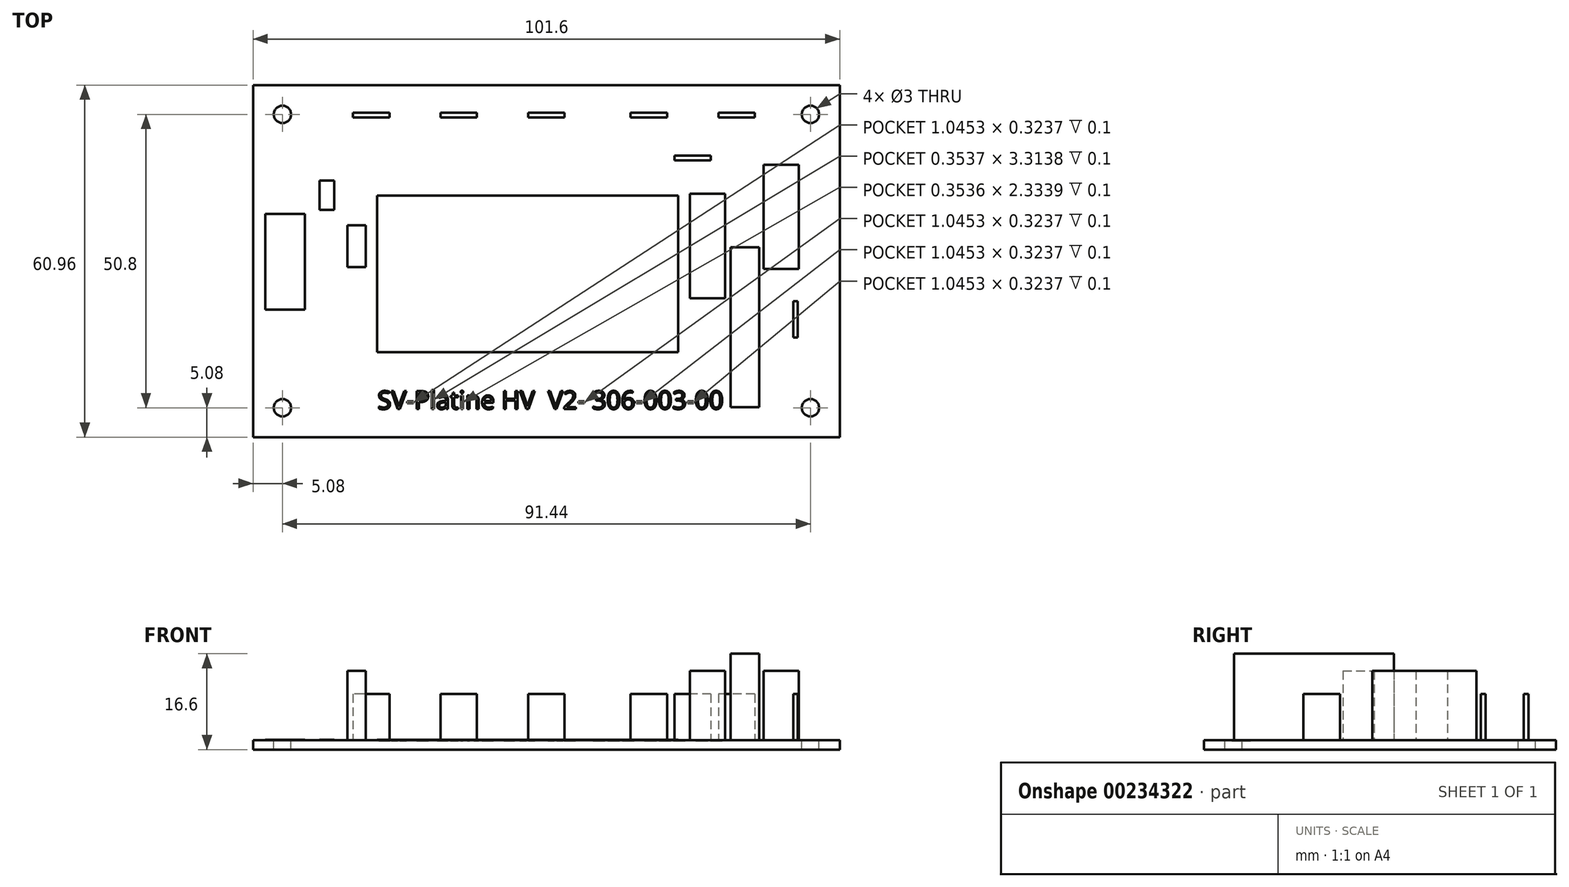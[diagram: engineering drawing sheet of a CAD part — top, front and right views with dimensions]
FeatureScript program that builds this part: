
annotation { "Feature Type Name" : "Feature", "Feature Type Description" : "" }
export const myFeature = defineFeature(function(context is Context, id is Id, definition is map)
    precondition{}
    {
        {
            var Q0;
            Q0=qCreatedBy(makeId("Top.planeOp"),FACE);
            var sketch = newSketch(context, id + "F0", { "sketchPlane" : qUnion([Q0])});
            skCircle(sketch, "E0", {"center": v(-45.72, -25.4) * mm, "radius": 1.5 * mm});
            skLineSegment(sketch, "E1.bottom", {"start": v(50.8, -30.48) * mm, "end": v(-50.8, -30.48) * mm});
            skLineSegment(sketch, "E1.top", {"start": v(50.8, 30.48) * mm, "end": v(-50.8, 30.48) * mm});
            skLineSegment(sketch, "E1.left", {"start": v(50.8, -30.48) * mm, "end": v(50.8, 30.48) * mm});
            skLineSegment(sketch, "E1.right", {"start": v(-50.8, -30.48) * mm, "end": v(-50.8, 30.48) * mm});
            skPoint(sketch, "E1.middle", {"position": v(0, 0) * mm});
            skCircle(sketch, "E2.MirrorC", {"center": v(45.72, -25.4) * mm, "radius": 1.5 * mm});
            skCircle(sketch, "E3.MirrorC", {"center": v(-45.72, 25.4) * mm, "radius": 1.5 * mm});
            skCircle(sketch, "E4.MirrorC", {"center": v(45.72, 25.4) * mm, "radius": 1.5 * mm});
            skLineSegment(sketch, "E5.bottom", {"start": v(-27.2, 24.88) * mm, "end": v(-33.5, 24.88) * mm});
            skLineSegment(sketch, "E5.top", {"start": v(-27.2, 25.68) * mm, "end": v(-33.5, 25.68) * mm});
            skLineSegment(sketch, "E5.left", {"start": v(-27.2, 24.88) * mm, "end": v(-27.2, 25.68) * mm});
            skLineSegment(sketch, "E5.right", {"start": v(-33.5, 24.88) * mm, "end": v(-33.5, 25.68) * mm});
            skPoint(sketch, "E5.middle", {"position": v(-30.34, 25.28) * mm});
            skLineSegment(sketch, "E6.bottom", {"start": v(-12.04, 24.88) * mm, "end": v(-18.34, 24.88) * mm});
            skLineSegment(sketch, "E6.top", {"start": v(-12.04, 25.68) * mm, "end": v(-18.34, 25.68) * mm});
            skLineSegment(sketch, "E6.left", {"start": v(-12.04, 24.88) * mm, "end": v(-12.04, 25.68) * mm});
            skLineSegment(sketch, "E6.right", {"start": v(-18.34, 24.88) * mm, "end": v(-18.34, 25.68) * mm});
            skPoint(sketch, "E6.middle", {"position": v(-15.19, 25.28) * mm});
            skLineSegment(sketch, "E7.bottom", {"start": v(3.15, 24.88) * mm, "end": v(-3.15, 24.88) * mm});
            skLineSegment(sketch, "E7.top", {"start": v(3.15, 25.68) * mm, "end": v(-3.15, 25.68) * mm});
            skLineSegment(sketch, "E7.left", {"start": v(3.15, 24.88) * mm, "end": v(3.15, 25.68) * mm});
            skLineSegment(sketch, "E7.right", {"start": v(-3.15, 24.88) * mm, "end": v(-3.15, 25.68) * mm});
            skPoint(sketch, "E7.middle", {"position": v(0, 25.28) * mm});
            skPoint(sketch, "E7.cornerSnap0", {"position": v(-15.19, 24.88) * mm});
            skLineSegment(sketch, "E8.bottom", {"start": v(20.87, 24.88) * mm, "end": v(14.57, 24.88) * mm});
            skLineSegment(sketch, "E8.top", {"start": v(20.87, 25.68) * mm, "end": v(14.57, 25.68) * mm});
            skLineSegment(sketch, "E8.left", {"start": v(20.87, 24.88) * mm, "end": v(20.87, 25.68) * mm});
            skLineSegment(sketch, "E8.right", {"start": v(14.57, 24.88) * mm, "end": v(14.57, 25.68) * mm});
            skPoint(sketch, "E8.middle", {"position": v(17.72, 25.28) * mm});
            skLineSegment(sketch, "E9.bottom", {"start": v(36.08, 24.88) * mm, "end": v(29.78, 24.88) * mm});
            skLineSegment(sketch, "E9.top", {"start": v(36.08, 25.68) * mm, "end": v(29.78, 25.68) * mm});
            skLineSegment(sketch, "E9.left", {"start": v(36.08, 24.88) * mm, "end": v(36.08, 25.68) * mm});
            skLineSegment(sketch, "E9.right", {"start": v(29.78, 24.88) * mm, "end": v(29.78, 25.68) * mm});
            skPoint(sketch, "E9.middle", {"position": v(32.93, 25.28) * mm});
            skLineSegment(sketch, "E10.bottom", {"start": v(28.49, 17.47) * mm, "end": v(22.19, 17.47) * mm});
            skLineSegment(sketch, "E10.top", {"start": v(28.49, 18.27) * mm, "end": v(22.19, 18.27) * mm});
            skLineSegment(sketch, "E10.left", {"start": v(28.49, 17.47) * mm, "end": v(28.49, 18.27) * mm});
            skLineSegment(sketch, "E10.right", {"start": v(22.19, 17.47) * mm, "end": v(22.19, 18.27) * mm});
            skPoint(sketch, "E10.middle", {"position": v(25.34, 17.87) * mm});
            skLineSegment(sketch, "E11.bottom", {"start": v(30.95, -6.44) * mm, "end": v(24.85, -6.44) * mm});
            skLineSegment(sketch, "E11.top", {"start": v(30.95, 11.65) * mm, "end": v(24.85, 11.65) * mm});
            skLineSegment(sketch, "E11.left", {"start": v(30.95, -6.44) * mm, "end": v(30.95, 11.65) * mm});
            skLineSegment(sketch, "E11.right", {"start": v(24.85, -6.44) * mm, "end": v(24.85, 11.65) * mm});
            skPoint(sketch, "E11.middle", {"position": v(27.9, 2.6) * mm});
            skLineSegment(sketch, "E12.bottom", {"start": v(43.7, -1.35) * mm, "end": v(37.6, -1.35) * mm});
            skLineSegment(sketch, "E12.top", {"start": v(43.7, 16.7) * mm, "end": v(37.6, 16.7) * mm});
            skLineSegment(sketch, "E12.left", {"start": v(43.7, -1.35) * mm, "end": v(43.7, 16.7) * mm});
            skLineSegment(sketch, "E12.right", {"start": v(37.6, -1.35) * mm, "end": v(37.6, 16.7) * mm});
            skPoint(sketch, "E12.middle", {"position": v(40.65, 7.67) * mm});
            skLineSegment(sketch, "E13.bottom", {"start": v(36.82, -25.29) * mm, "end": v(31.88, -25.29) * mm});
            skLineSegment(sketch, "E13.top", {"start": v(36.82, 2.42) * mm, "end": v(31.88, 2.42) * mm});
            skLineSegment(sketch, "E13.left", {"start": v(36.82, -25.29) * mm, "end": v(36.82, 2.42) * mm});
            skLineSegment(sketch, "E13.right", {"start": v(31.88, -25.29) * mm, "end": v(31.88, 2.42) * mm});
            skPoint(sketch, "E13.middle", {"position": v(34.35, -11.43) * mm});
            skLineSegment(sketch, "E14.bottom", {"start": v(43.53, -13.25) * mm, "end": v(42.73, -13.25) * mm});
            skLineSegment(sketch, "E14.top", {"start": v(43.53, -6.95) * mm, "end": v(42.73, -6.95) * mm});
            skLineSegment(sketch, "E14.left", {"start": v(43.53, -13.25) * mm, "end": v(43.53, -6.95) * mm});
            skLineSegment(sketch, "E14.right", {"start": v(42.73, -13.25) * mm, "end": v(42.73, -6.95) * mm});
            skPoint(sketch, "E14.middle", {"position": v(43.13, -10.1) * mm});
            skLineSegment(sketch, "E15.bottom", {"start": v(-31.27, -1.06) * mm, "end": v(-34.5, -1.06) * mm});
            skLineSegment(sketch, "E15.top", {"start": v(-31.27, 6.2) * mm, "end": v(-34.5, 6.2) * mm});
            skLineSegment(sketch, "E15.left", {"start": v(-31.27, -1.06) * mm, "end": v(-31.27, 6.2) * mm});
            skLineSegment(sketch, "E15.right", {"start": v(-34.5, -1.06) * mm, "end": v(-34.5, 6.2) * mm});
            skPoint(sketch, "E15.middle", {"position": v(-32.88, 2.57) * mm});
            skLineSegment(sketch, "E16.bottom", {"start": v(-48.67, 8.16) * mm, "end": v(-41.82, 8.16) * mm});
            skLineSegment(sketch, "E16.top", {"start": v(-48.67, -8.4) * mm, "end": v(-41.82, -8.4) * mm});
            skLineSegment(sketch, "E16.left", {"start": v(-48.67, 8.16) * mm, "end": v(-48.67, -8.4) * mm});
            skLineSegment(sketch, "E16.right", {"start": v(-41.82, 8.16) * mm, "end": v(-41.82, -8.4) * mm});
            skLineSegment(sketch, "E17.bottom", {"start": v(-29.36, 11.37) * mm, "end": v(22.79, 11.37) * mm});
            skLineSegment(sketch, "E17.top", {"start": v(-29.36, -15.77) * mm, "end": v(22.79, -15.77) * mm});
            skLineSegment(sketch, "E17.left", {"start": v(-29.36, 11.37) * mm, "end": v(-29.36, -15.77) * mm});
            skLineSegment(sketch, "E17.right", {"start": v(22.79, 11.37) * mm, "end": v(22.79, -15.77) * mm});
            skLineSegment(sketch, "E18.bottom", {"start": v(-36.73, 8.85) * mm, "end": v(-39.27, 8.85) * mm});
            skLineSegment(sketch, "E18.top", {"start": v(-36.73, 13.93) * mm, "end": v(-39.27, 13.93) * mm});
            skLineSegment(sketch, "E18.left", {"start": v(-36.73, 8.85) * mm, "end": v(-36.73, 13.93) * mm});
            skLineSegment(sketch, "E18.right", {"start": v(-39.27, 8.85) * mm, "end": v(-39.27, 13.93) * mm});
            skPoint(sketch, "E18.middle", {"position": v(-38, 11.39) * mm});
            skSolve(sketch);
        }
        {
            var Q0;
            Q0=makeQuery(id+"F0.imprint","IMPRINT",FACE,{"disambiguationData":[TD([[makeQuery(id+"F0.imprint","IMPRINT",EDGE,{"derivedFrom":sQuery(id+"F0.wireOp",EDGE,"E0")}),-1.0]])]});
            var Q1;
            Q1=makeQuery(id+"F0.imprint","IMPRINT",FACE,{"disambiguationData":[TD([[makeQuery(id+"F0.imprint","IMPRINT",EDGE,{"derivedFrom":sQuery(id+"F0.wireOp",EDGE,"E16.bottom")}),-1.0]])]});
            var Q2;
            Q2=makeQuery(id+"F0.imprint","IMPRINT",FACE,{"disambiguationData":[TD([[makeQuery(id+"F0.imprint","IMPRINT",EDGE,{"derivedFrom":sQuery(id+"F0.wireOp",EDGE,"E15.bottom")}),-1.0]])]});
            var Q3;
            Q3=makeQuery(id+"F0.imprint","IMPRINT",FACE,{"disambiguationData":[TD([[makeQuery(id+"F0.imprint","IMPRINT",EDGE,{"derivedFrom":sQuery(id+"F0.wireOp",EDGE,"E17.bottom")}),-1.0]])]});
            var Q4;
            Q4=makeQuery(id+"F0.imprint","IMPRINT",FACE,{"disambiguationData":[TD([[makeQuery(id+"F0.imprint","IMPRINT",EDGE,{"derivedFrom":sQuery(id+"F0.wireOp",EDGE,"E11.bottom")}),-1.0]])]});
            var Q5;
            Q5=makeQuery(id+"F0.imprint","IMPRINT",FACE,{"disambiguationData":[TD([[makeQuery(id+"F0.imprint","IMPRINT",EDGE,{"derivedFrom":sQuery(id+"F0.wireOp",EDGE,"E13.bottom")}),-1.0]])]});
            var Q6;
            Q6=makeQuery(id+"F0.imprint","IMPRINT",FACE,{"disambiguationData":[TD([[makeQuery(id+"F0.imprint","IMPRINT",EDGE,{"derivedFrom":sQuery(id+"F0.wireOp",EDGE,"E12.bottom")}),-1.0]])]});
            var Q7;
            Q7=makeQuery(id+"F0.imprint","IMPRINT",FACE,{"disambiguationData":[TD([[makeQuery(id+"F0.imprint","IMPRINT",EDGE,{"derivedFrom":sQuery(id+"F0.wireOp",EDGE,"E5.bottom")}),-1.0]])]});
            var Q8;
            Q8=makeQuery(id+"F0.imprint","IMPRINT",FACE,{"disambiguationData":[TD([[makeQuery(id+"F0.imprint","IMPRINT",EDGE,{"derivedFrom":sQuery(id+"F0.wireOp",EDGE,"E6.bottom")}),-1.0]])]});
            var Q9;
            Q9=makeQuery(id+"F0.imprint","IMPRINT",FACE,{"disambiguationData":[TD([[makeQuery(id+"F0.imprint","IMPRINT",EDGE,{"derivedFrom":sQuery(id+"F0.wireOp",EDGE,"E7.bottom")}),-1.0]])]});
            var Q10;
            Q10=makeQuery(id+"F0.imprint","IMPRINT",FACE,{"disambiguationData":[TD([[makeQuery(id+"F0.imprint","IMPRINT",EDGE,{"derivedFrom":sQuery(id+"F0.wireOp",EDGE,"E8.bottom")}),-1.0]])]});
            var Q11;
            Q11=makeQuery(id+"F0.imprint","IMPRINT",FACE,{"disambiguationData":[TD([[makeQuery(id+"F0.imprint","IMPRINT",EDGE,{"derivedFrom":sQuery(id+"F0.wireOp",EDGE,"E9.bottom")}),-1.0]])]});
            var Q12;
            Q12=makeQuery(id+"F0.imprint","IMPRINT",FACE,{"disambiguationData":[TD([[makeQuery(id+"F0.imprint","IMPRINT",EDGE,{"derivedFrom":sQuery(id+"F0.wireOp",EDGE,"E10.bottom")}),-1.0]])]});
            var Q13;
            Q13=makeQuery(id+"F0.imprint","IMPRINT",FACE,{"disambiguationData":[TD([[makeQuery(id+"F0.imprint","IMPRINT",EDGE,{"derivedFrom":sQuery(id+"F0.wireOp",EDGE,"E14.bottom")}),-1.0]])]});
            var Q14;
            Q14=makeQuery(id+"F0.imprint","IMPRINT",FACE,{"disambiguationData":[TD([[makeQuery(id+"F0.imprint","IMPRINT",EDGE,{"derivedFrom":sQuery(id+"F0.wireOp",EDGE,"E18.bottom")}),-1.0]])]});
            extrude(context, id + "F1", {"entities" : qUnion([Q0, Q1, Q2, Q3, Q4, Q5, Q6, Q7, Q8, Q9, Q10, Q11, Q12, Q13, Q14]), "oppositeDirection" : true, "depth" : 1.6 * mm, "offsetDistance" : 25 * mm});
        }
        {
            var Q0;
            Q0=makeQuery(id+"F1.opExtrude","CAP_FACE",FACE,{"disambiguationData":[OSD([sQuery(id+"F0.wireOp",EDGE,"LsjD8Xkw-FGJJ-3g42-Yrlz-kK8atOvaHSqe.bottom"),sQuery(id+"F0.wireOp",EDGE,"LsjD8Xkw-FGJJ-3g42-Yrlz-kK8atOvaHSqe.top"),sQuery(id+"F0.wireOp",EDGE,"LsjD8Xkw-FGJJ-3g42-Yrlz-kK8atOvaHSqe.left"),sQuery(id+"F0.wireOp",EDGE,"LsjD8Xkw-FGJJ-3g42-Yrlz-kK8atOvaHSqe.right"),sQuery(id+"F0.wireOp",EDGE,"E0"),sQuery(id+"F0.wireOp",EDGE,"8424d585-6a70-4b2f-b95d-e58967aeadfe0.MirrorC")])],"isStart":true});
            var sketch = newSketch(context, id + "F2", { "sketchPlane" : qUnion([Q0])});
            skText(sketch, "E19", { "text": "SV-Platine HV  V2- 306-003-00", "fontName": "OpenSans-Regular.ttf"});
            const initialGuessF2  = {"E19": [-0.02926, -0.02562, 1, 0, 0.00314]};
            skSetInitialGuess(sketch, initialGuessF2);
            skSolve(sketch);
        }
        {
            var Q0;
            Q0=qSketchRegion(id+"F2",true);
            extrude(context, id + "F3", {"entities" : qUnion([Q0]), "operationType" : NewBodyOperationType.REMOVE, "oppositeDirection" : true, "depth" : .1 * mm});
        }
        {
            var Q0;
            Q0=makeQuery(id+"F0.imprint","IMPRINT",FACE,{"disambiguationData":[TD([[makeQuery(id+"F0.imprint","IMPRINT",EDGE,{"derivedFrom":sQuery(id+"F0.wireOp",EDGE,"E7.bottom")}),-1.0]])]});
            var Q1;
            Q1=makeQuery(id+"F0.imprint","IMPRINT",FACE,{"disambiguationData":[TD([[makeQuery(id+"F0.imprint","IMPRINT",EDGE,{"derivedFrom":sQuery(id+"F0.wireOp",EDGE,"E8.bottom")}),-1.0]])]});
            var Q2;
            Q2=makeQuery(id+"F0.imprint","IMPRINT",FACE,{"disambiguationData":[TD([[makeQuery(id+"F0.imprint","IMPRINT",EDGE,{"derivedFrom":sQuery(id+"F0.wireOp",EDGE,"E9.bottom")}),-1.0]])]});
            var Q3;
            Q3=makeQuery(id+"F0.imprint","IMPRINT",FACE,{"disambiguationData":[TD([[makeQuery(id+"F0.imprint","IMPRINT",EDGE,{"derivedFrom":sQuery(id+"F0.wireOp",EDGE,"E10.bottom")}),-1.0]])]});
            var Q4;
            Q4=makeQuery(id+"F0.imprint","IMPRINT",FACE,{"disambiguationData":[TD([[makeQuery(id+"F0.imprint","IMPRINT",EDGE,{"derivedFrom":sQuery(id+"F0.wireOp",EDGE,"E14.bottom")}),-1.0]])]});
            var Q5;
            Q5=makeQuery(id+"F0.imprint","IMPRINT",FACE,{"disambiguationData":[TD([[makeQuery(id+"F0.imprint","IMPRINT",EDGE,{"derivedFrom":sQuery(id+"F0.wireOp",EDGE,"E6.bottom")}),-1.0]])]});
            var Q6;
            Q6=makeQuery(id+"F0.imprint","IMPRINT",FACE,{"disambiguationData":[TD([[makeQuery(id+"F0.imprint","IMPRINT",EDGE,{"derivedFrom":sQuery(id+"F0.wireOp",EDGE,"E5.bottom")}),-1.0]])]});
            extrude(context, id + "F4", {"entities" : qUnion([Q0, Q1, Q2, Q3, Q4, Q5, Q6]), "depth" : 8 * mm, "offsetDistance" : 25 * mm});
        }
        {
            var Q0;
            Q0=makeQuery(id+"F0.imprint","IMPRINT",FACE,{"disambiguationData":[TD([[makeQuery(id+"F0.imprint","IMPRINT",EDGE,{"derivedFrom":sQuery(id+"F0.wireOp",EDGE,"E11.bottom")}),-1.0]])]});
            var Q1;
            Q1=makeQuery(id+"F0.imprint","IMPRINT",FACE,{"disambiguationData":[TD([[makeQuery(id+"F0.imprint","IMPRINT",EDGE,{"derivedFrom":sQuery(id+"F0.wireOp",EDGE,"E12.bottom")}),-1.0]])]});
            var Q2;
            Q2=makeQuery(id+"F0.imprint","IMPRINT",FACE,{"disambiguationData":[TD([[makeQuery(id+"F0.imprint","IMPRINT",EDGE,{"derivedFrom":sQuery(id+"F0.wireOp",EDGE,"E15.bottom")}),-1.0]])]});
            extrude(context, id + "F5", {"entities" : qUnion([Q0, Q1, Q2]), "operationType" : NewBodyOperationType.ADD, "depth" : 12 * mm, "offsetDistance" : 25 * mm});
        }
        {
            var Q0;
            Q0=makeQuery(id+"F0.imprint","IMPRINT",FACE,{"disambiguationData":[TD([[makeQuery(id+"F0.imprint","IMPRINT",EDGE,{"derivedFrom":sQuery(id+"F0.wireOp",EDGE,"E13.bottom")}),-1.0]])]});
            extrude(context, id + "F6", {"entities" : qUnion([Q0]), "depth" : 15 * mm, "offsetDistance" : 25 * mm});
        }
        {
            var Q0;
            Q0=makeQuery(id+"F0.imprint","IMPRINT",FACE,{"disambiguationData":[TD([[makeQuery(id+"F0.imprint","IMPRINT",EDGE,{"derivedFrom":sQuery(id+"F0.wireOp",EDGE,"E16.bottom")}),-1.0]])]});
            var Q1;
            Q1=makeQuery(id+"F0.imprint","IMPRINT",FACE,{"disambiguationData":[TD([[makeQuery(id+"F0.imprint","IMPRINT",EDGE,{"derivedFrom":sQuery(id+"F0.wireOp",EDGE,"E18.bottom")}),-1.0]])]});
            var Q2;
            Q2=makeQuery(id+"F0.imprint","IMPRINT",FACE,{"disambiguationData":[TD([[makeQuery(id+"F0.imprint","IMPRINT",EDGE,{"derivedFrom":sQuery(id+"F0.wireOp",EDGE,"E17.bottom")}),-1.0]])]});
            extrude(context, id + "F7", {"entities" : qUnion([Q0, Q1, Q2]), "operationType" : NewBodyOperationType.ADD, "depth" : .1 * mm, "offsetDistance" : 25 * mm});
        }
    });
